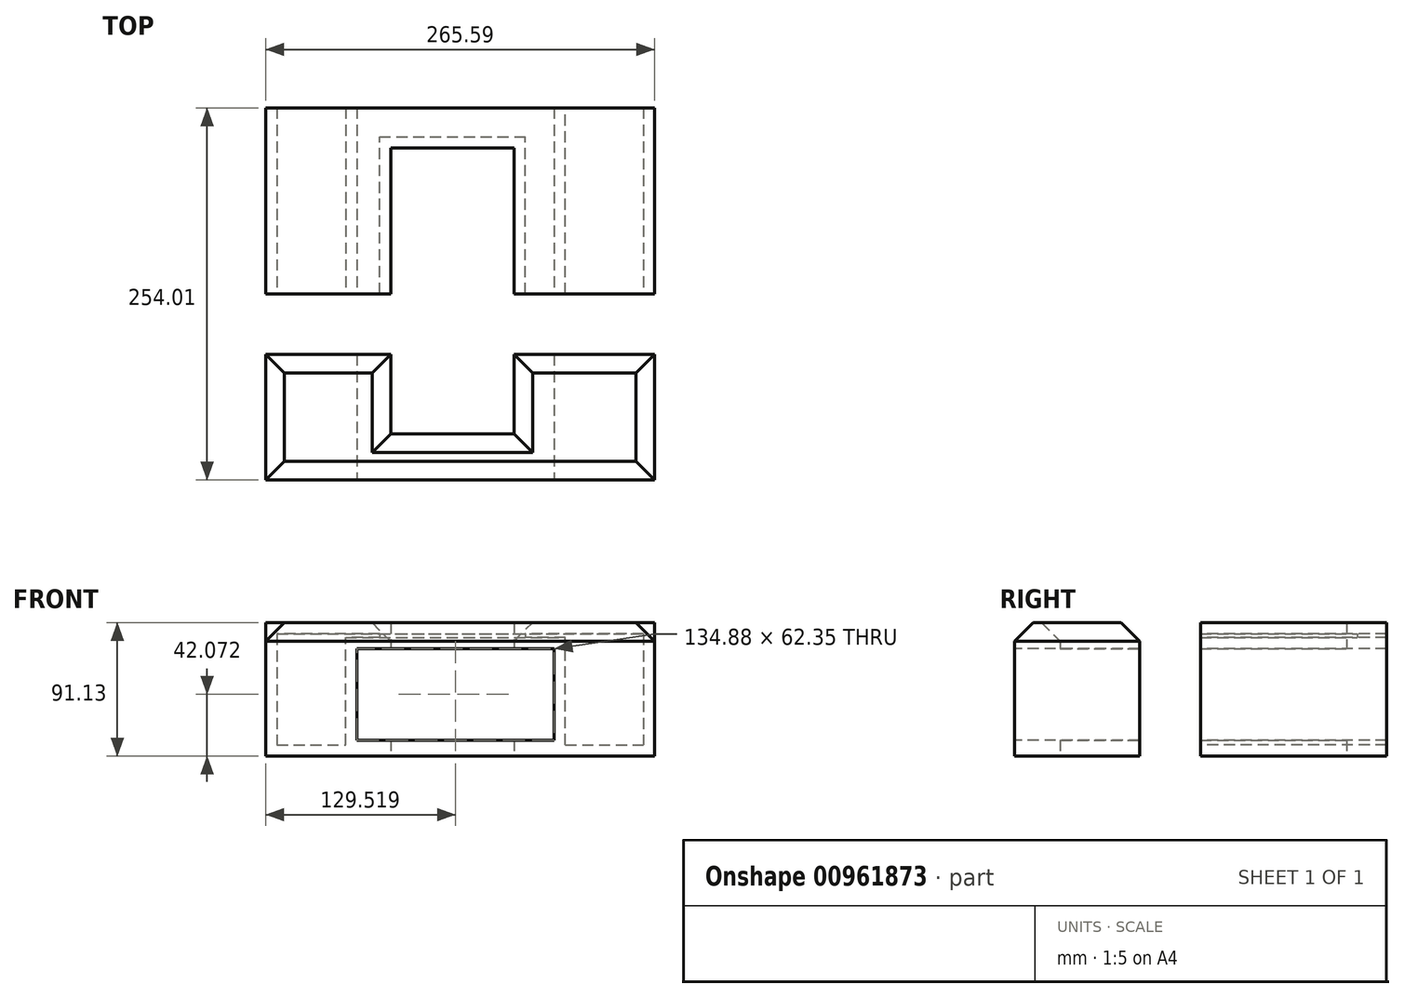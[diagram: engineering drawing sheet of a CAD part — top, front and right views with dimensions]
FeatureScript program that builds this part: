
annotation { "Feature Type Name" : "Feature", "Feature Type Description" : "" }
export const myFeature = defineFeature(function(context is Context, id is Id, definition is map)
    precondition{}
    {
        {
            var Q0;
            Q0=qCreatedBy(makeId("Top.planeOp"),FACE);
            var sketch = newSketch(context, id + "F0", { "sketchPlane" : qUnion([Q0])});
            skLineSegment(sketch, "E0.bottom", {"start": v(-63.96, -43.13) * mm, "end": v(20.17, -43.13) * mm});
            skLineSegment(sketch, "E0.top", {"start": v(-63.96, 152.18) * mm, "end": v(20.17, 152.18) * mm});
            skLineSegment(sketch, "E0.left", {"start": v(-63.96, -43.13) * mm, "end": v(-63.96, 152.18) * mm});
            skLineSegment(sketch, "E0.right", {"start": v(20.17, -43.13) * mm, "end": v(20.17, 152.18) * mm});
            skPoint(sketch, "E0.middle", {"position": v(-21.9, 54.52) * mm});
            skLineSegment(sketch, "E1.bottom", {"start": v(-149.32, 179.55) * mm, "end": v(116.27, 179.55) * mm});
            skLineSegment(sketch, "E1.top", {"start": v(-149.32, -74.46) * mm, "end": v(116.27, -74.46) * mm});
            skLineSegment(sketch, "E1.left", {"start": v(-149.32, 179.55) * mm, "end": v(-149.32, -74.46) * mm});
            skLineSegment(sketch, "E1.right", {"start": v(116.27, 179.55) * mm, "end": v(116.27, -74.46) * mm});
            skLineSegment(sketch, "E2.bottom", {"start": v(116.27, 11.18) * mm, "end": v(-149.32, 11.18) * mm});
            skLineSegment(sketch, "E2.top", {"start": v(116.27, 52.54) * mm, "end": v(-149.32, 52.54) * mm});
            skLineSegment(sketch, "E2.left", {"start": v(116.27, 11.18) * mm, "end": v(116.27, 52.54) * mm});
            skLineSegment(sketch, "E2.right", {"start": v(-149.32, 11.18) * mm, "end": v(-149.32, 52.54) * mm});
            skSolve(sketch);
        }
        {
            var Q0;
            {var subQ2=sQuery(id+"F0.wireOp",EDGE,"E0.bottom");Q0=makeQuery(id+"F0.imprint","IMPRINT",FACE,{"disambiguationData":[TD([[makeQuery(id+"F0.imprint","IMPRINT",EDGE,{"derivedFrom":subQ2}),-1.0]])]});}
            var Q1;
            {var subQ7=sQuery(id+"F0.wireOp",EDGE,"E0.top");Q1=makeQuery(id+"F0.imprint","IMPRINT",FACE,{"disambiguationData":[TD([[makeQuery(id+"F0.imprint","IMPRINT",EDGE,{"derivedFrom":subQ7}),1.0]])]});}
            extrude(context, id + "F1", {"entities" : qUnion([Q0, Q1]), "depth" : 91.13 * mm, "offsetDistance" : 25.4 * mm});
        }
        {
            var Q0;
            {var subQ0=sQuery(id+"F0.wireOp",EDGE,"E1.right");Q0=makeQuery(id+"F1.opExtrude","CAP_EDGE",EDGE,{"disambiguationData":[OSD([subQ0]),TDD([makeQuery(id+"F0.imprint","IMPRINT",EDGE,{"disambiguationData":[TD([[makeQuery(id+"F0.imprint","INTERSECT",VERTEX,{"derivedFrom":[sQuery(id+"F0.wireOp",EDGE,"E1.top"),subQ0]}),1.0]])],"derivedFrom":subQ0})])],"isStart":false});}
            var Q1;
            Q1=makeQuery(id+"F1.opExtrude","CAP_EDGE",EDGE,{"disambiguationData":[OSD([sQuery(id+"F0.wireOp",EDGE,"E1.top")])],"isStart":false});
            var Q2;
            {var subQ0=sQuery(id+"F0.wireOp",EDGE,"E2.bottom");Q2=makeQuery(id+"F1.opExtrude","CAP_EDGE",EDGE,{"disambiguationData":[OSD([subQ0]),TDD([makeQuery(id+"F0.imprint","IMPRINT",EDGE,{"disambiguationData":[TD([[makeQuery(id+"F0.imprint","INTERSECT",VERTEX,{"derivedFrom":[sQuery(id+"F0.wireOp",EDGE,"E0.right"),subQ0]}),1.0]])],"derivedFrom":subQ0})])],"isStart":false});}
            var Q3;
            {var subQ0=sQuery(id+"F0.wireOp",EDGE,"E0.right");Q3=makeQuery(id+"F1.opExtrude","CAP_EDGE",EDGE,{"disambiguationData":[OSD([subQ0]),TDD([makeQuery(id+"F0.imprint","IMPRINT",EDGE,{"disambiguationData":[TD([[makeQuery(id+"F0.imprint","INTERSECT",VERTEX,{"derivedFrom":[sQuery(id+"F0.wireOp",EDGE,"E0.bottom"),subQ0]}),-1.0]])],"derivedFrom":subQ0})])],"isStart":false});}
            var Q4;
            Q4=makeQuery(id+"F1.opExtrude","CAP_EDGE",EDGE,{"disambiguationData":[OSD([sQuery(id+"F0.wireOp",EDGE,"E0.bottom")])],"isStart":false});
            var Q5;
            {var subQ0=sQuery(id+"F0.wireOp",EDGE,"E0.left");Q5=makeQuery(id+"F1.opExtrude","CAP_EDGE",EDGE,{"disambiguationData":[OSD([subQ0]),TDD([makeQuery(id+"F0.imprint","IMPRINT",EDGE,{"disambiguationData":[TD([[makeQuery(id+"F0.imprint","INTERSECT",VERTEX,{"derivedFrom":[sQuery(id+"F0.wireOp",EDGE,"E0.bottom"),subQ0]}),-1.0]])],"derivedFrom":subQ0})])],"isStart":false});}
            var Q6;
            {var subQ0=sQuery(id+"F0.wireOp",EDGE,"E2.bottom");Q6=makeQuery(id+"F1.opExtrude","CAP_EDGE",EDGE,{"disambiguationData":[OSD([subQ0]),TDD([makeQuery(id+"F0.imprint","IMPRINT",EDGE,{"disambiguationData":[TD([[makeQuery(id+"F0.imprint","INTERSECT",VERTEX,{"derivedFrom":[sQuery(id+"F0.wireOp",EDGE,"E0.left"),subQ0]}),-1.0]])],"derivedFrom":subQ0})])],"isStart":false});}
            var Q7;
            {var subQ0=sQuery(id+"F0.wireOp",EDGE,"E1.left");Q7=makeQuery(id+"F1.opExtrude","CAP_EDGE",EDGE,{"disambiguationData":[OSD([subQ0]),TDD([makeQuery(id+"F0.imprint","IMPRINT",EDGE,{"disambiguationData":[TD([[makeQuery(id+"F0.imprint","INTERSECT",VERTEX,{"derivedFrom":[sQuery(id+"F0.wireOp",EDGE,"E1.top"),subQ0]}),1.0]])],"derivedFrom":subQ0})])],"isStart":false});}
            chamfer(context, id + "F2", {"entities" : qUnion([Q0, Q1, Q2, Q3, Q4, Q5, Q6, Q7]), "width" : 12.7 * mm, "tangentPropagation" : true});
        }
        {
            var Q0;
            Q0=makeQuery(id+"F1.opExtrude","SWEPT_FACE",FACE,{"disambiguationData":[OSD([sQuery(id+"F0.wireOp",EDGE,"E1.top")])]});
            var sketch = newSketch(context, id + "F3", { "sketchPlane" : qUnion([Q0])});
            skLineSegment(sketch, "E3.bottom", {"start": v(47.64, 73.24) * mm, "end": v(-87.24, 73.24) * mm});
            skLineSegment(sketch, "E3.top", {"start": v(47.64, 10.9) * mm, "end": v(-87.24, 10.9) * mm});
            skLineSegment(sketch, "E3.left", {"start": v(47.64, 73.24) * mm, "end": v(47.64, 10.9) * mm});
            skLineSegment(sketch, "E3.right", {"start": v(-87.24, 73.24) * mm, "end": v(-87.24, 10.9) * mm});
            skSolve(sketch);
        }
        {
            var Q0;
            Q0=makeQuery(id+"F3.imprint","IMPRINT",FACE,{"disambiguationData":[TD([[makeQuery(id+"F3.imprint","IMPRINT",EDGE,{"derivedFrom":sQuery(id+"F3.wireOp",EDGE,"E3.bottom")}),1.0]])]});
            extrude(context, id + "F4", {"entities" : qUnion([Q0]), "operationType" : NewBodyOperationType.REMOVE, "oppositeDirection" : true, "depth" : 408.08 * mm, "offsetDistance" : 25.4 * mm});
        }
        {
            var Q0;
            {var subQ0=sQuery(id+"F0.wireOp",EDGE,"E2.top");Q0=makeQuery(id+"F1.opExtrude","SWEPT_FACE",FACE,{"disambiguationData":[OSD([subQ0]),TDD([makeQuery(id+"F0.imprint","IMPRINT",EDGE,{"disambiguationData":[TD([[makeQuery(id+"F0.imprint","INTERSECT",VERTEX,{"derivedFrom":[sQuery(id+"F0.wireOp",EDGE,"E0.right"),subQ0]}),1.0]])],"derivedFrom":subQ0})])]});}
            var Q1;
            {var subQ0=sQuery(id+"F0.wireOp",EDGE,"E2.top");Q1=makeQuery(id+"F1.opExtrude","SWEPT_FACE",FACE,{"disambiguationData":[OSD([subQ0]),TDD([makeQuery(id+"F0.imprint","IMPRINT",EDGE,{"disambiguationData":[TD([[makeQuery(id+"F0.imprint","INTERSECT",VERTEX,{"derivedFrom":[sQuery(id+"F0.wireOp",EDGE,"E0.left"),subQ0]}),-1.0]])],"derivedFrom":subQ0})])]});}
            var Q2;
            Q2=makeQuery(id+"F1.opExtrude","SWEPT_FACE",FACE,{"disambiguationData":[OSD([sQuery(id+"F0.wireOp",EDGE,"E1.bottom")])]});
            shell(context, id + "F5", {"entities" : qUnion([Q0, Q1, Q2]), "thickness" : 7.62 * mm});
        }
    });
